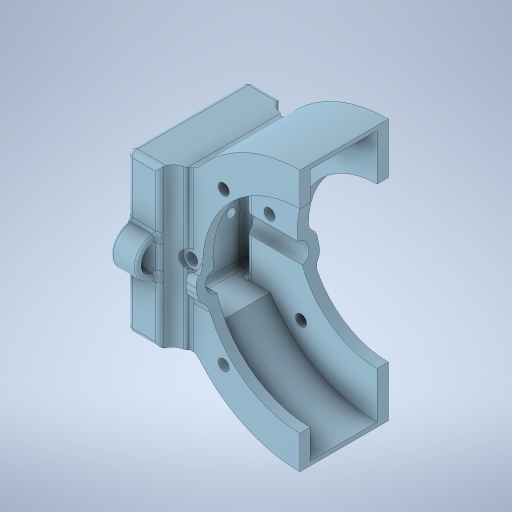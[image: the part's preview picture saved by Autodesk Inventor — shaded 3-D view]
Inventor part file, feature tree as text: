
AUTODESK INVENTOR PART (.ipt)
format: ipt  version: 2023.2 (Build 272271000, 271)  size: 819,712 bytes
history: native  units: in
note: dims shown in document units (in); Inventor stores cm internally (conversion verified against a paired STEP export)
features: sketch x18, extrude x16, fillet x8, projected_geometry x8, revolve x1
ambient origin geometry x8: Origin, YZ Plane, XZ Plane, XY Plane, X Axis, Y Axis, Z Axis, Center Point
bodies: Solid1 (feature_tree), Body1 (feature_tree)
feature tree (51):
  sketch  "Boceto1"  dims[d0=0.0187in d1=0.0in d2=2.4409in]
  extrude  "Extrusión1"  Depth=2.4409in
  extrude  "Extrusión2"  Depth=0.3937in
  extrude  "Extrusión3"  Depth=0.2756in
  sketch  "Boceto8"  dims[d23=0.1181in d24=0.0in d25=2.4724in d26=0.0394in]
  extrude  "Extrusión5"  Depth=0.2756in
  revolve  "Revolución1"  [1 undecoded]
  fillet  "Empalme5"  Radius=0.0394in
  sketch  "Boceto15"  dims[d35=0.0787in d36=0.0787in]
  sketch  "Boceto16"  dims[d37=0.0787in d38=0.0787in d39=1.1811in d40=0.0in d41=0.2756in d42=1.1811in d43=0.0in d44=0.2756in]
  extrude  "Extrusión6"  Depth=0.0524in TaperAngle=0.0deg
  extrude  "Extrusión7"  Depth=0.0524in TaperAngle=0.0deg
  extrude  "Extrusión8"  Depth=0.0787in
  extrude  "Extrusión9"  Depth=0.0787in
  fillet  "Empalme6"  Radius=1.1811in
  fillet  "Empalme7"  Radius=0.2756in
  fillet  "Empalme8"  Radius=1.1811in
  fillet  "Empalme9"  Radius=0.2756in
  extrude  "Extrusión10"  Depth=0.3937in TaperAngle=0.0deg
  extrude  "Extrusión12"  Depth=0.1575in
  extrude  "Extrusión11"  Depth=0.1181in TaperAngle=0.0deg
  extrude  "Extrusión13"  Depth=0.2756in
  extrude  "Extrusión14"  Depth=0.2756in
  fillet  "Empalme10"  Radius=0.1181in
  extrude  "Extrusión15"  Depth=0.0787in
  fillet  "Empalme11"  Radius=1.9685in
  extrude  "Extrusión16"  Depth=1.9685in
  extrude  "Extrusión17"  [1 undecoded]
  fillet  "Empalme12"  [1 undecoded]
  sketch  "Boceto3"  dims[d3=0.3937in d4=0.0in d5=3.7795in]
  projected_geometry  "Contorno proyectado1"
  sketch  "Boceto4"  dims[d14=0.0394in d15=0.0in d18=0.2756in]
  sketch  "Boceto7"  dims[d19=0.2756in d20=0.2756in]
  projected_geometry  "Contorno proyectado3"
  sketch  "Boceto9"  dims[d27=0.0524in d28=0.0in d29=0.0524in d30=0.0in]
  projected_geometry  "Contorno proyectado4"
  sketch  "Boceto14"  dims[d31=0.0524in d32=0.0in d33=0.0524in d34=0.0in]
  projected_geometry  "Contorno proyectado8"
  projected_geometry  "Contorno proyectado9"
  projected_geometry  "Contorno proyectado10"
  sketch  "Boceto17"  dims[d45=1.1811in d46=0.0in d47=0.3937in d48=0.0in]
  projected_geometry  "Contorno proyectado11"
  sketch  "Boceto18"  dims[d49=0.1181in d50=0.0in d51=0.1575in]
  projected_geometry  "Contorno proyectado12"
  sketch  "Boceto19"  dims[d52=0.1378in d53=0.1181in d54=0.0in]
  sketch  "Boceto20"  dims[d55=0.1575in d56=0.2756in]
  sketch  "Boceto22"  dims[d57=0.1181in d58=0.0in d59=0.2756in d60=0.1181in d61=0.0in]
  sketch  "Boceto24"  dims[d62=0.0787in d12=0.0197in d13=1.9685in]
  sketch  "Boceto25"  dims[d16=0.0197in d17=1.9685in]
  sketch  "Boceto26"
  sketch  "Boceto27"
note: 3 required parameter values undecoded (feature->parameter linkage not recoverable at this tier; creation-order binding heuristic only, values carry confidence <= 0.55)